# Revit family: External Joint Retrofit
name_source: partatom
category: Specialty Equipment
units: mm (PartAtom-declared; Revit-internal decimal feet)

## family parameters
Cut with Voids When Loaded = No
OmniClass Number = 23.10.00.00
OmniClass Title = Site Products
Part Type = Normal
Room Calculation Point = No
Round Connector Dimension = Use Diameter
Shared = No

## types (2) — shared parameters
Assembly Code = F1030
Certifications = NSF 61, NSF 372, CRD C-572-74, ASTM D484
Description = JP500 is Earth Shield thermoplastic vulcanizate "L"-shaped external-applied, retrofit waterstop. Chemical, UV, fuel and ozone resistant. Includes all (40) s/s Tapcons and s/s bar.
Edition number = 1
Height = 0.31 "
Hydrophilic = No
Hydrophobic = Yes
Keynote = 13000
Manufacturer = J P Specialties Inc.
Materials = TPV
Model = JP500
Product Guid = 27e5cdcc-cece-4d8c-947d-ca6b8ef269ba
Product Material = JP Specialties - Polyvinyl Chloride (PVC)
Product data url = www.bimmodeller.com/jpspecialties/products/Polyvinyl-Chloride-PVC-Waterstop
Telephone = 951-763-7077
URL = https://www.jpspecialties.com
Weight = 2 lbs/lft
Width = 9 "

## per-type parameters (varying)
| type | z_Horizontal | z_Vertical |
| JP500- Horizontal | Yes | No |
| JP500 - Vertical | No | Yes |

## geometry (parser evidence)
native form markers: Sweep x4
no freeform markers — native parametric forms only
